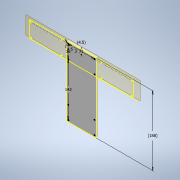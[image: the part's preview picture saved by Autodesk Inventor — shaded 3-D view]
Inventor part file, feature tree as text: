
AUTODESK INVENTOR PART (.ipt)
format: ipt  version: 2021 (Build 250183000, 183)  size: 145,920 bytes
history: native  units: mm
features: extrude x3, sketch x3, plane x2, reference x2, projected_geometry x2, other x2
ambient origin geometry x8: Origin, YZ Plane, XZ Plane, XY Plane, X Axis, Y Axis, Z Axis, Center Point
bodies: Solid1 (feature_tree)
feature tree (14):
  plane  "Work Plane1"
  extrude  "Extrusion1"  Depth=80.0mm
  sketch  "Sketch2"  dims[d2=5.0mm d3=0.0mm d4=5.0mm d5=0.0mm]
  plane  "Work Plane2"
  extrude  "Extrusion2"  Depth=5.0mm TaperAngle=0.0deg
  extrude  "Extrusion3"  Depth=10.0mm
  sketch  "Sketch1"  dims[d0=80.0mm d1=46.0mm]
  reference  "Reference1"
  projected_geometry  "Projected Loop1"
  sketch  "Sketch3"  dims[d6=4.500001mm d7=4.5mm d8=3.0mm d9=20.0mm d11=71.0mm d12=20.0mm d14=36.0mm d17=188.0mm d18=20.0mm d20=143.0mm d21=10.0mm d23=10.0mm d25=0.0mm d26=0.0mm d19=0.5mm]
  reference  "Reference2"
  projected_geometry  "Projected Loop2"
  other  "4_WheelsSwerve01.iam"
  other  "Part10:2"
